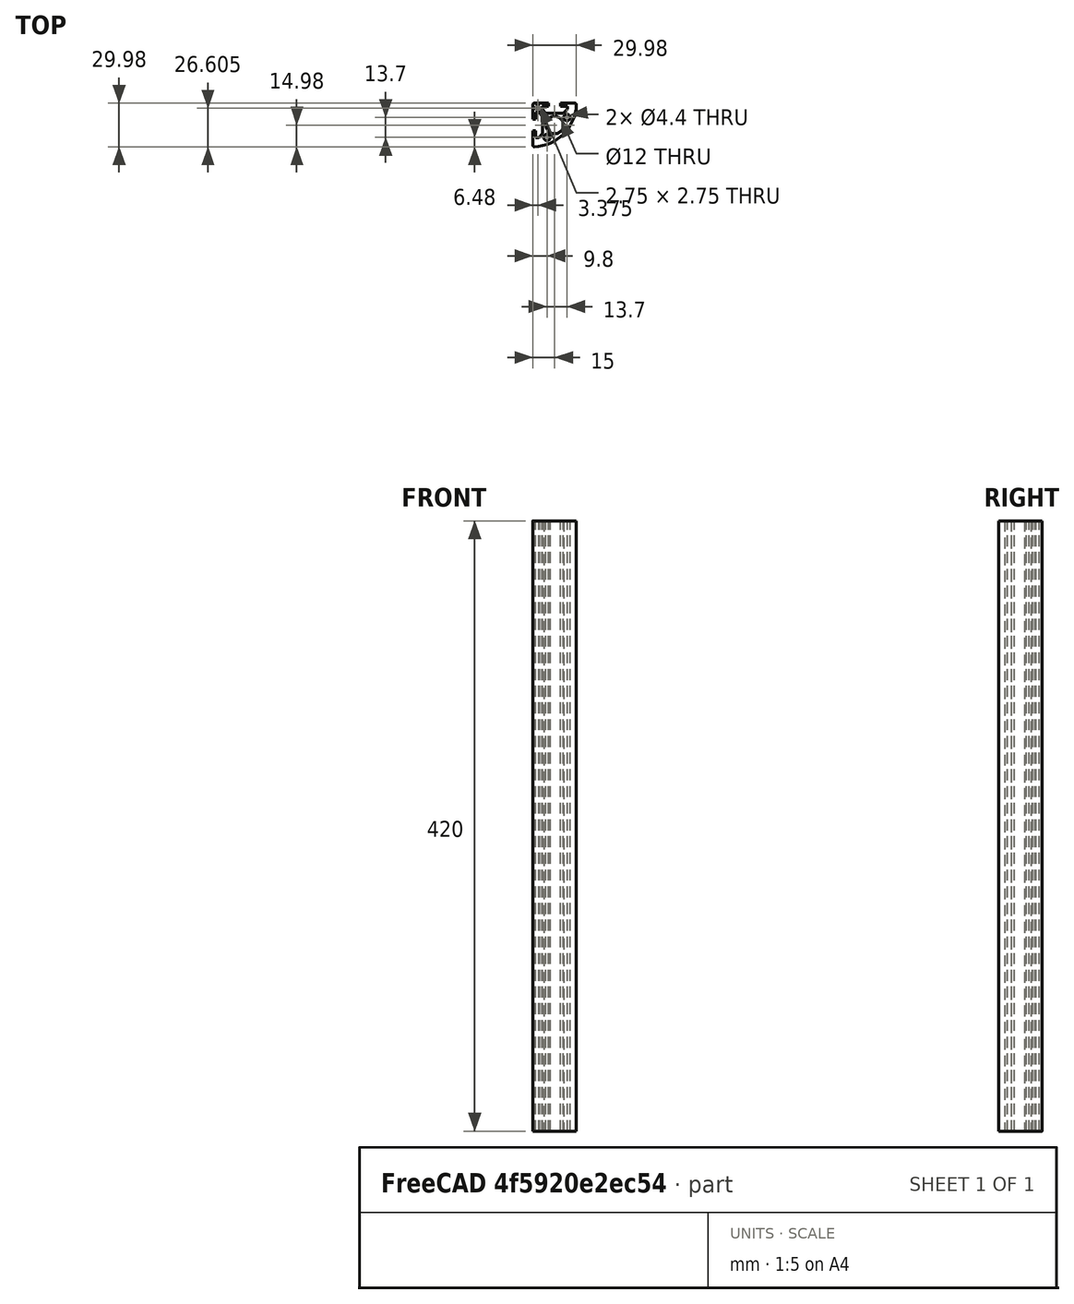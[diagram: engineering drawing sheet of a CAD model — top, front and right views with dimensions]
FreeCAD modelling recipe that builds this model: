
FCSTD DOCUMENT  (FreeCAD 0.17R13387 (Git))
Label: Z-Profile_3030_rounded
License: All rights reserved
LicenseURL: http://en.wikipedia.org/wiki/All_rights_reserved
objects: Sketcher::SketchObject×1, PartDesign::Pad×1, PartDesign::Body×1
note: 4 computed .brp shape members not serialized (recipe doc carries the construction recipe); baked Part::Feature solids carry a one-line shape summary decoded from their .brp

FEATURE [Sketcher::SketchObject] Sketch006
  sketch-geometry (33):
    g0: LineSegment StartX=13.9828 StartY=15 StartZ=0 EndX=4.1 EndY=15 EndZ=0
    g1: LineSegment StartX=4.1 StartY=15 StartZ=0 EndX=4.1 EndY=13 EndZ=0
    g2: LineSegment StartX=4.1 StartY=13 StartZ=0 EndX=8.75 EndY=13 EndZ=0
    g3: LineSegment StartX=8.75 StartY=13 StartZ=0 EndX=8.75 EndY=11 EndZ=0
    g4: LineSegment StartX=8.75 StartY=11 StartZ=0 EndX=6 EndY=8.25 EndZ=0
    g5: LineSegment StartX=6 StartY=8.25 StartZ=0 EndX=-6 EndY=8.25 EndZ=0
    g6: LineSegment StartX=-6 StartY=8.25 StartZ=0 EndX=-8.75 EndY=11 EndZ=0
    g7: LineSegment StartX=-8.75 StartY=11 StartZ=0 EndX=-8.75 EndY=13 EndZ=0
    g8: LineSegment StartX=-8.75 StartY=13 StartZ=0 EndX=-4.1 EndY=13 EndZ=0
    g9: LineSegment StartX=-4.1 StartY=13 StartZ=0 EndX=-4.1 EndY=15 EndZ=0
    g10: LineSegment StartX=-4.1 StartY=15 StartZ=0 EndX=-14 EndY=15 EndZ=0
    g11: ArcOfCircle CenterX=-14 CenterY=14 CenterZ=0 NormalX=0 NormalY=0 NormalZ=1 AngleXU=-3.14159 Radius=1 StartAngle=4.71239 EndAngle=6.28319
    g12: LineSegment StartX=-15 StartY=14 StartZ=0 EndX=-15 EndY=4.1 EndZ=0
    g13: LineSegment StartX=-15 StartY=4.1 StartZ=0 EndX=-13 EndY=4.1 EndZ=0
    g14: LineSegment StartX=-13 StartY=4.1 StartZ=0 EndX=-13 EndY=8.75 EndZ=0
    g15: LineSegment StartX=-13 StartY=8.75 StartZ=0 EndX=-11 EndY=8.75 EndZ=0
    g16: LineSegment StartX=-11 StartY=8.75 StartZ=0 EndX=-8.25 EndY=6 EndZ=0
    g17: LineSegment StartX=-8.25 StartY=6 StartZ=0 EndX=-8.25 EndY=-6 EndZ=0
    g18: LineSegment StartX=-8.25 StartY=-6 StartZ=0 EndX=-11 EndY=-8.75 EndZ=0
    g19: LineSegment StartX=-11 StartY=-8.75 StartZ=0 EndX=-13 EndY=-8.75 EndZ=0
    g20: LineSegment StartX=-13 StartY=-8.75 StartZ=0 EndX=-13 EndY=-4.1 EndZ=0
    g21: LineSegment StartX=-13 StartY=-4.1 StartZ=0 EndX=-15 EndY=-4.1 EndZ=0
    g22: LineSegment StartX=-15 StartY=-4.1 StartZ=0 EndX=-15 EndY=-13.9828 EndZ=0
    g23: LineSegment StartX=-13 StartY=13 StartZ=0 EndX=-10.25 EndY=13 EndZ=0
    g24: LineSegment StartX=-10.25 StartY=13 StartZ=0 EndX=-10.25 EndY=10.25 EndZ=0
    g25: LineSegment StartX=-10.25 StartY=10.25 StartZ=0 EndX=-13 EndY=10.25 EndZ=0
    g26: LineSegment StartX=-13 StartY=10.25 StartZ=0 EndX=-13 EndY=13 EndZ=0
    g27: ArcOfCircle CenterX=-15 CenterY=15 CenterZ=0 NormalX=0 NormalY=0 NormalZ=1 AngleXU=0 Radius=30 StartAngle=4.74688 EndAngle=6.2487
    g28: ArcOfCircle CenterX=-14 CenterY=-13.9828 CenterZ=0 NormalX=0 NormalY=0 NormalZ=1 AngleXU=0 Radius=1 StartAngle=3.14159 EndAngle=4.74688
    g29: ArcOfCircle CenterX=13.9828 CenterY=14 CenterZ=0 NormalX=0 NormalY=0 NormalZ=1 AngleXU=0 Radius=1 StartAngle=6.2487 EndAngle=7.85398
    g30: Circle CenterX=0 CenterY=0 CenterZ=0 NormalX=0 NormalY=0 NormalZ=1 AngleXU=0 Radius=6
    g31: Circle CenterX=-5.2 CenterY=-8.5 CenterZ=0 NormalX=0 NormalY=0 NormalZ=1 AngleXU=0 Radius=2.2
    g32: Circle CenterX=8.5 CenterY=5.2 CenterZ=0 NormalX=0 NormalY=0 NormalZ=1 AngleXU=0 Radius=2.2
  constraints (102):
    c: Coincident(g1,g2)
    c: Horizontal(g2)
    c: Coincident(g2,g3)
    c: Coincident(g3,g4)
    c: Horizontal(g5)
    c: Coincident(g5,g6)
    c: Coincident(g6,g7)
    c: Coincident(g7,g8)
    c: Horizontal(g8)
    c: Coincident(g8,g9)
    c: Horizontal(g13)
    c: Coincident(g13,g14)
    c: Coincident(g14,g15)
    c: Coincident(g15,g16)
    c: Vertical(g17)
    c: Horizontal(g21)
    c: Vertical(g12)
    c: DistanceX(g11) = -15
    c: DistanceY(g10) = 15
    c: Horizontal(g10)
    c: Vertical(g1)
    c: Vertical(g9)
    c: DistanceX(g8,g1) = 8.2
    c: Radius(g11) = 1
    c: Coincident(g10,g9)
    c: Horizontal(g0)
    c: Coincident(g0,g1)
    c: Coincident(g13,g12)
    c: Parallel(g6,g16)
    c: Horizontal(g15)
    c: Vertical(g14)
    c: Vertical(g7)
    c: Vertical(g3)
    c: Equal(g14,g8)
    c: Equal(g8,g2)
    c: Equal(g15,g7)
    c: Equal(g7,g3)
    c: Equal(g13,g9)
    c: Equal(g9,g1)
    c: DistanceX(g13,g13) = 2
    c: DistanceY(g19,g14) = 17.5
    c: Equal(g3,g7)
    c: Equal(g7,g15)
    c: DistanceX(g16,g-1) = 8.25
    c: Coincident(g17,g16)
    c: Coincident(g17,g18)
    c: Coincident(g19,g18)
    c: DistanceY(g-1,g5) = 8.25
    c: Equal(g12,g10)
    c: Coincident(g5,g4)
    c: Equal(g17,g5)
    c: Equal(g13,g21)
    c: Coincident(g19,g20)
    c: Horizontal(g19)
    c: Vertical(g20)
    c: Coincident(g20,g21)
    c: Coincident(g21,g22)
    c: Vertical(g22)
    c: PointOnObject(g21,g12)
    c: Coincident(g23,g24)
    c: Coincident(g24,g25)
    c: Coincident(g25,g26)
    c: Coincident(g26,g23)
    c: Horizontal(g23)
    c: Horizontal(g25)
    c: Vertical(g24)
    c: Vertical(g26)
    c: Equal(g23,g24)
    c: Symmetric(g5,g4,g-2)
    c: Symmetric(g17,g16,g-1)
    c: DistanceX(g7,g2) = 17.5
    c: Tangent(g10,g11) = -1.5708
    c: Tangent(g11,g12) = -1.5708
    c: DistanceX(g27) = -15
    c: DistanceY(g27) = 15
    c: Radius(g27) = 30
    c: DistanceY(g0) = 15
    c: DistanceX(g0) = 4.1
    c: Tangent(g28,g27) = -1.5708
    c: Tangent(g28,g22) = -1.5708
    c: Tangent(g29,g0) = -1.5708
    c: Tangent(g29,g27) = -1.5708
    c: Coincident(g30,g-1)
    c: Radius(g30) = 6
    c: Equal(g22,g0)
    c: Equal(g28,g29)
    c: Radius(g29) = 1
    c: Equal(g7,g3)
    c: Equal(g3,g15)
    c: Equal(g15,g19)
    c: Equal(g4,g6)
    c: DistanceX(g24) = -10.25
    c: DistanceY(g24) = 10.25
    c: DistanceY(g26,g26) = 2.75
    c: Equal(g26,g23)
    c: Equal(g25,g24)
    c: DistanceX(g32) = 8.5
    c: DistanceY(g32) = 5.2
    c: DistanceX(g31) = -5.2
    c: DistanceY(g31) = -8.5
    c: Radius(g31) = 2.2
    c: Equal(g31,g32)
FEATURE [PartDesign::Pad] Pad
  Length = 420
  Length2 = 100
  Profile = -> Sketch006
  Type = 0
FEATURE [PartDesign::Body] Body
  Group = -> [Sketch006,Pad]
  Origin = -> Origin
  Tip = -> Pad
